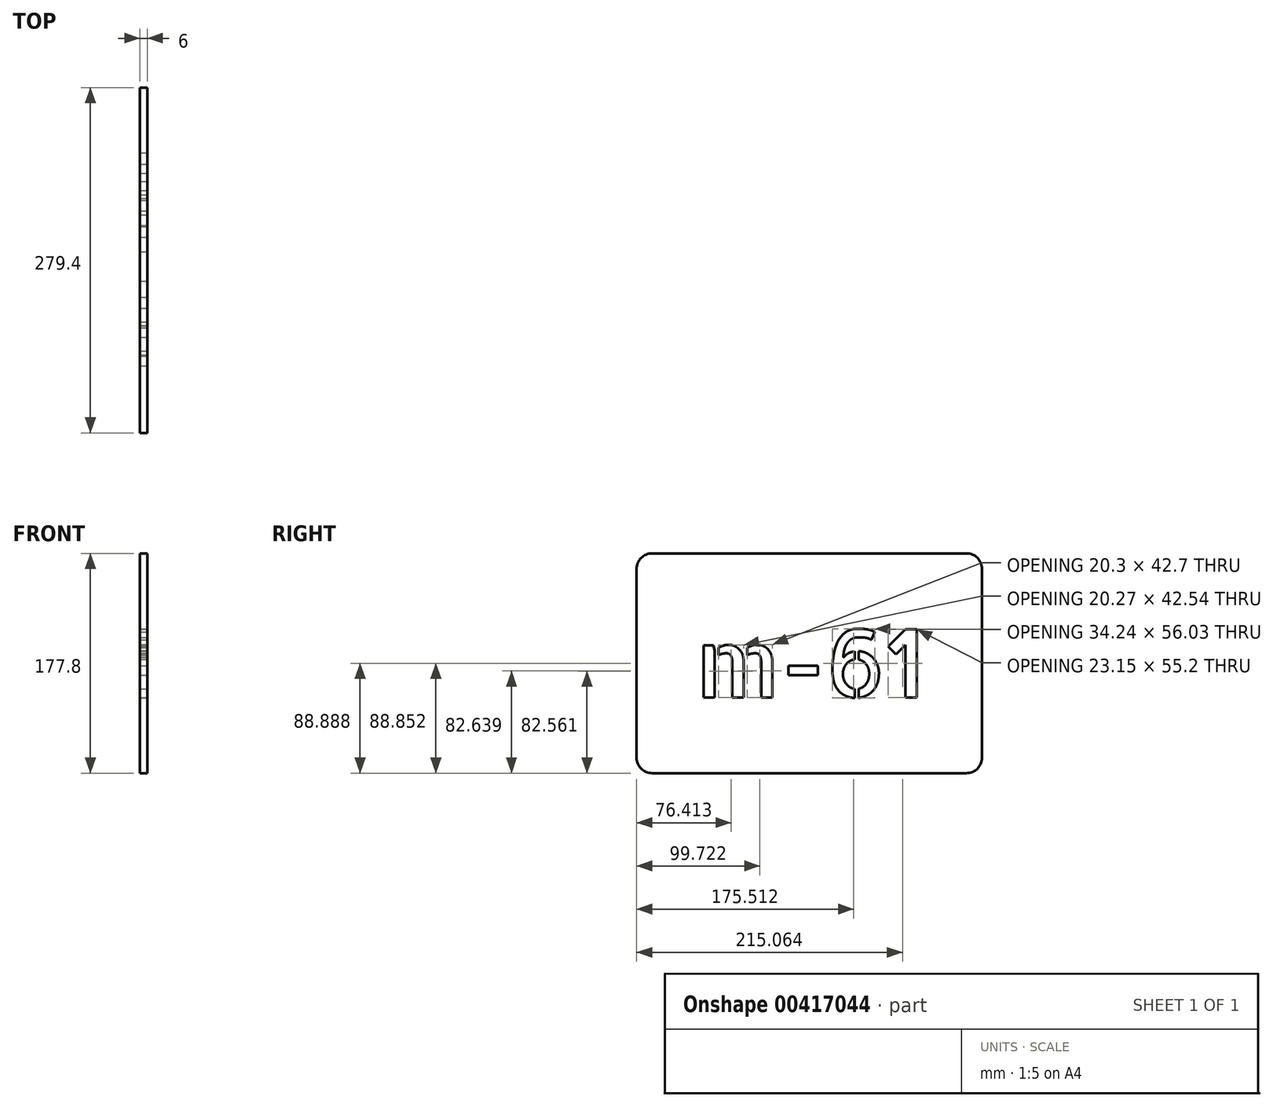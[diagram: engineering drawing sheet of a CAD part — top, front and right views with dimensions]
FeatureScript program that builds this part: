
annotation { "Feature Type Name" : "Feature", "Feature Type Description" : "" }
export const myFeature = defineFeature(function(context is Context, id is Id, definition is map)
    precondition{}
    {
        {
            var Q0;
            Q0=qCreatedBy(makeId("Right.planeOp"),FACE);
            var sketch = newSketch(context, id + "F0", { "sketchPlane" : qUnion([Q0])});
            skLineSegment(sketch, "E0.bottom", {"start": v(-127, 88.9) * mm, "end": v(127, 88.9) * mm});
            skLineSegment(sketch, "E0.top", {"start": v(-127, -88.9) * mm, "end": v(127, -88.9) * mm});
            skLineSegment(sketch, "E0.left", {"start": v(-139.7, 76.2) * mm, "end": v(-139.7, -76.2) * mm});
            skLineSegment(sketch, "E0.right", {"start": v(139.7, 76.2) * mm, "end": v(139.7, -76.2) * mm});
            skPoint(sketch, "E1.visualSharp", {"position": v(-139.7, 88.9) * mm});
            skArc(sketch, "E1.filletArc", {"start": v(-127, 88.9) * mm, "mid": v(-135.98, 85.18) * mm, "end": v(-139.7, 76.2) * mm});
            skPoint(sketch, "E2.visualSharp", {"position": v(139.7, 88.9) * mm});
            skArc(sketch, "E2.filletArc", {"start": v(139.7, 76.2) * mm, "mid": v(135.98, 85.18) * mm, "end": v(127, 88.9) * mm});
            skPoint(sketch, "E3.visualSharp", {"position": v(139.7, -88.9) * mm});
            skArc(sketch, "E3.filletArc", {"start": v(127, -88.9) * mm, "mid": v(135.98, -85.18) * mm, "end": v(139.7, -76.2) * mm});
            skPoint(sketch, "E4.visualSharp", {"position": v(-139.7, -88.9) * mm});
            skArc(sketch, "E4.filletArc", {"start": v(-139.7, -76.2) * mm, "mid": v(-135.98, -85.18) * mm, "end": v(-127, -88.9) * mm});
            skPoint(sketch, "E5.endSnap0", {"position": v(139.7, 0) * mm});
            skLineSegment(sketch, "E6", {"start": v(0, 88.9) * mm, "end": v(0, 0) * mm, "construction": true});
            skLineSegment(sketch, "E7", {"start": v(0, 0) * mm, "end": v(139.7, 0) * mm, "construction": true});
            skSolve(sketch);
        }
        {
            var Q0;
            Q0=makeQuery(id+"F0.imprint","IMPRINT",FACE,{"disambiguationData":[TD([[makeQuery(id+"F0.imprint","IMPRINT",EDGE,{"derivedFrom":sQuery(id+"F0.wireOp",EDGE,"E0.bottom")}),-1.0]])]});
            extrude(context, id + "F1", {"entities" : qUnion([Q0]), "depth" : 6 * mm});
        }
        {
            var Q0;
            Q0=makeQuery(id+"F1.opExtrude","CAP_FACE",FACE,{"disambiguationData":[OSD([sQuery(id+"F0.wireOp",EDGE,"E0.bottom"),sQuery(id+"F0.wireOp",EDGE,"E0.top"),sQuery(id+"F0.wireOp",EDGE,"E0.left"),sQuery(id+"F0.wireOp",EDGE,"E0.right"),sQuery(id+"F0.wireOp",EDGE,"E1.filletArc"),sQuery(id+"F0.wireOp",EDGE,"E2.filletArc"),sQuery(id+"F0.wireOp",EDGE,"E3.filletArc"),sQuery(id+"F0.wireOp",EDGE,"E4.filletArc")])],"isStart":false});
            var sketch = newSketch(context, id + "F2", { "sketchPlane" : qUnion([Q0])});
            skText(sketch, "E8", { "text": "m-61", "fontName": "AllertaStencil-Regular.ttf"});
            skLineSegment(sketch, "E9", {"start": v(-92.07, 0) * mm, "end": v(-139.7, 0) * mm, "construction": true});
            skLineSegment(sketch, "E10", {"start": v(0, 27.61) * mm, "end": v(0, 88.9) * mm, "construction": true});
            const initialGuessF2  = {"E8": [-0.09207, -0.02761, 1, 0, 0.05522]};
            skSetInitialGuess(sketch, initialGuessF2);
            skSolve(sketch);
        }
        {
            var Q0;
            Q0 = qSketchRegion(id + "F2", true);
            var Q1;
            Q1=makeQuery(id+"F0.imprint","IMPRINT",FACE,{"disambiguationData":[TD([[makeQuery(id+"F0.imprint","IMPRINT",EDGE,{"derivedFrom":sQuery(id+"F0.wireOp",EDGE,"E0.bottom")}),-1.0]])]});
            extrude(context, id + "F3", {"entities" : qUnion([Q0, Q1]), "operationType" : NewBodyOperationType.REMOVE, "oppositeDirection" : true, "depth" : 25.4 * mm});
        }
    });
